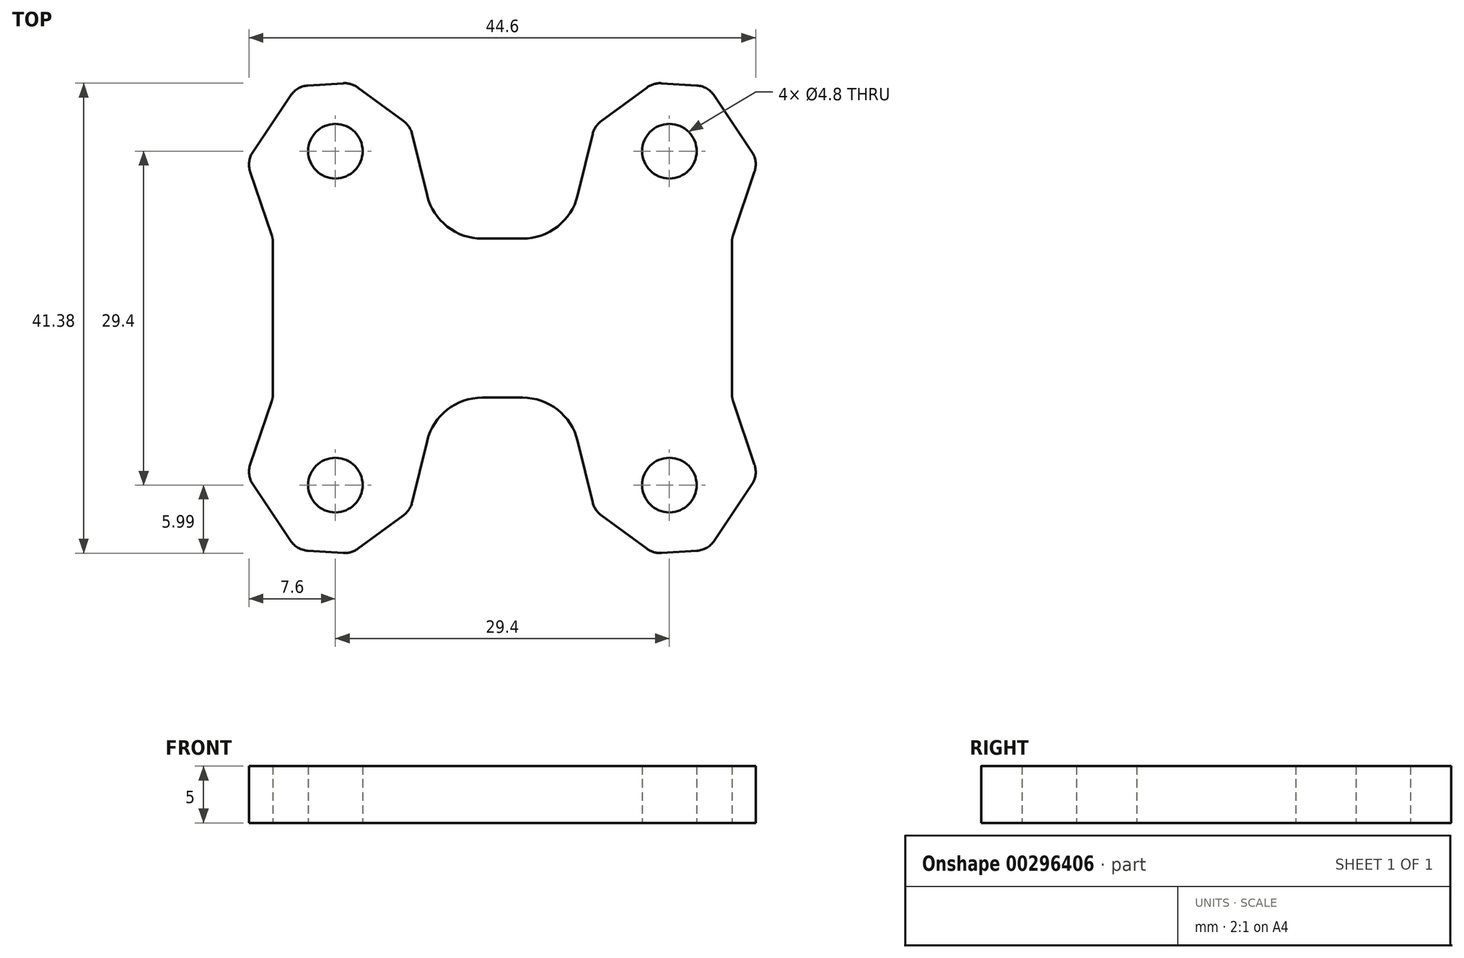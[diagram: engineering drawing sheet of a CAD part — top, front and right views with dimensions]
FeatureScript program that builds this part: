
annotation { "Feature Type Name" : "Feature", "Feature Type Description" : "" }
export const myFeature = defineFeature(function(context is Context, id is Id, definition is map)
    precondition{}
    {
        {
            var Q0;
            Q0=qCreatedBy(makeId("Top.planeOp"),FACE);
            var sketch = newSketch(context, id + "F0", { "sketchPlane" : qUnion([Q0])});
            skLineSegment(sketch, "E0.bottom", {"start": v(14.7, -14.7) * mm, "end": v(-14.7, -14.7) * mm, "construction": true});
            skLineSegment(sketch, "E0.top", {"start": v(14.7, 14.7) * mm, "end": v(-14.7, 14.7) * mm, "construction": true});
            skLineSegment(sketch, "E0.left", {"start": v(14.7, -14.7) * mm, "end": v(14.7, 14.7) * mm, "construction": true});
            skLineSegment(sketch, "E0.right", {"start": v(-14.7, -14.7) * mm, "end": v(-14.7, 14.7) * mm, "construction": true});
            skPoint(sketch, "E0.middle", {"position": v(0, 0) * mm});
            skLineSegment(sketch, "E1", {"start": v(-14.7, 5) * mm, "end": v(14.7, 5) * mm, "construction": true});
            skLineSegment(sketch, "E2.MirrorCS", {"start": v(-14.7, -5) * mm, "end": v(14.7, -5) * mm, "construction": true});
            skCircle(sketch, "E3", {"center": v(14.7, 14.7) * mm, "radius": 2.5 * mm, "construction": true});
            skCircle(sketch, "E4", {"center": v(14.7, 14.7) * mm, "radius": 9.7 * mm, "construction": true});
            skCircle(sketch, "E5.MirrorC", {"center": v(14.7, -14.7) * mm, "radius": 2.5 * mm, "construction": true});
            skCircle(sketch, "E6.MirrorC", {"center": v(14.7, -14.7) * mm, "radius": 9.7 * mm, "construction": true});
            skCircle(sketch, "E7.MirrorC", {"center": v(-14.7, 14.7) * mm, "radius": 9.7 * mm, "construction": true});
            skCircle(sketch, "E8.MirrorC", {"center": v(-14.7, 14.7) * mm, "radius": 2.5 * mm, "construction": true});
            skCircle(sketch, "E9.MirrorC", {"center": v(-14.7, -14.7) * mm, "radius": 9.7 * mm, "construction": true});
            skCircle(sketch, "E10.MirrorC", {"center": v(-14.7, -14.7) * mm, "radius": 2.5 * mm, "construction": true});
            skLineSegment(sketch, "E11", {"start": v(0, 7) * mm, "end": v(5.7, 7) * mm});
            skLineSegment(sketch, "E12", {"start": v(5.7, 7) * mm, "end": v(9.11, 21) * mm});
            skLineSegment(sketch, "E13", {"start": v(9.11, 21) * mm, "end": v(24.6, 20) * mm});
            skLineSegment(sketch, "E14", {"start": v(24.6, 20) * mm, "end": v(20.2, 7) * mm});
            skLineSegment(sketch, "E15", {"start": v(20.2, 7) * mm, "end": v(20.2, 0) * mm});
            skLineSegment(sketch, "E16", {"start": v(20.2, 0) * mm, "end": v(0, 0) * mm});
            skLineSegment(sketch, "E17", {"start": v(0, 7) * mm, "end": v(0, 0) * mm});
            skCircle(sketch, "E18", {"center": v(14.7, 14.7) * mm, "radius": 2.4 * mm});
            skSolve(sketch);
        }
        {
            var Q0;
            Q0=makeQuery(id+"F0.imprint","IMPRINT",FACE,{"disambiguationData":[TD([[makeQuery(id+"F0.imprint","IMPRINT",EDGE,{"derivedFrom":sQuery(id+"F0.wireOp",EDGE,"E11")}),-1.0]])]});
            extrude(context, id + "F1", {"entities" : qUnion([Q0]), "depth" : 5 * mm, "offsetDistance" : 25 * mm});
        }
        {
            var Q0;
            Q0=makeQuery(id+"F1.opExtrude","SWEPT_BODY",BODY,{"disambiguationData":[OSD([sQuery(id+"F0.wireOp",EDGE,"E11"),sQuery(id+"F0.wireOp",EDGE,"E12"),sQuery(id+"F0.wireOp",EDGE,"E13"),sQuery(id+"F0.wireOp",EDGE,"E14"),sQuery(id+"F0.wireOp",EDGE,"E15"),sQuery(id+"F0.wireOp",EDGE,"E16"),sQuery(id+"F0.wireOp",EDGE,"E17"),sQuery(id+"F0.wireOp",EDGE,"E18")])]});
            var Q1;
            Q1=makeQuery(id+"F1.opExtrude","SWEPT_FACE",FACE,{"disambiguationData":[OSD([sQuery(id+"F0.wireOp",EDGE,"E16")])]});
            mirror(context, id + "F2", {"operationType" : NewBodyOperationType.ADD, "entities" : qUnion([Q0]), "mirrorPlane" : qUnion([Q1])});
        }
        {
            var Q0;
            Q0=makeQuery(id+"F1.opExtrude","SWEPT_BODY",BODY,{"disambiguationData":[OSD([sQuery(id+"F0.wireOp",EDGE,"E11"),sQuery(id+"F0.wireOp",EDGE,"E12"),sQuery(id+"F0.wireOp",EDGE,"E13"),sQuery(id+"F0.wireOp",EDGE,"E14"),sQuery(id+"F0.wireOp",EDGE,"E15"),sQuery(id+"F0.wireOp",EDGE,"E16"),sQuery(id+"F0.wireOp",EDGE,"E17"),sQuery(id+"F0.wireOp",EDGE,"E18")])]});
            var Q1;
            {var subQ0=makeQuery(id+"F1.opExtrude","SWEPT_FACE",FACE,{"disambiguationData":[OSD([sQuery(id+"F0.wireOp",EDGE,"E17")])]});Q1=makeQuery(id+"F2.boolean.opBoolean","MERGE",FACE,{"derivedFrom":[subQ0,makeQuery(id+"F2.opPattern","COPY",FACE,{"derivedFrom":subQ0,"instanceName":"1"})]});}
            mirror(context, id + "F3", {"operationType" : NewBodyOperationType.ADD, "entities" : qUnion([Q0]), "mirrorPlane" : qUnion([Q1])});
        }
        {
            var Q0;
            Q0=makeQuery(id+"F1.opExtrude","SWEPT_EDGE",EDGE,{"disambiguationData":[OSD([sQuery(id+"F0.wireOp",EDGE,"E13"),sQuery(id+"F0.wireOp",EDGE,"E14")])]});
            var Q1;
            Q1=makeQuery(id+"F2.opPattern","COPY",EDGE,{"derivedFrom":makeQuery(id+"F1.opExtrude","SWEPT_EDGE",EDGE,{"disambiguationData":[OSD([sQuery(id+"F0.wireOp",EDGE,"E13"),sQuery(id+"F0.wireOp",EDGE,"E14")])]}),"instanceName":"1"});
            var Q2;
            Q2=makeQuery(id+"F2.opPattern","COPY",EDGE,{"derivedFrom":makeQuery(id+"F1.opExtrude","SWEPT_EDGE",EDGE,{"disambiguationData":[OSD([sQuery(id+"F0.wireOp",EDGE,"E12"),sQuery(id+"F0.wireOp",EDGE,"E13")])]}),"instanceName":"1"});
            var Q3;
            Q3=makeQuery(id+"F3.opPattern","COPY",EDGE,{"derivedFrom":makeQuery(id+"F2.opPattern","COPY",EDGE,{"derivedFrom":makeQuery(id+"F1.opExtrude","SWEPT_EDGE",EDGE,{"disambiguationData":[OSD([sQuery(id+"F0.wireOp",EDGE,"E12"),sQuery(id+"F0.wireOp",EDGE,"E13")])]}),"instanceName":"1"}),"instanceName":"1"});
            var Q4;
            Q4=makeQuery(id+"F3.opPattern","COPY",EDGE,{"derivedFrom":makeQuery(id+"F2.opPattern","COPY",EDGE,{"derivedFrom":makeQuery(id+"F1.opExtrude","SWEPT_EDGE",EDGE,{"disambiguationData":[OSD([sQuery(id+"F0.wireOp",EDGE,"E13"),sQuery(id+"F0.wireOp",EDGE,"E14")])]}),"instanceName":"1"}),"instanceName":"1"});
            var Q5;
            Q5=makeQuery(id+"F3.opPattern","COPY",EDGE,{"derivedFrom":makeQuery(id+"F1.opExtrude","SWEPT_EDGE",EDGE,{"disambiguationData":[OSD([sQuery(id+"F0.wireOp",EDGE,"E13"),sQuery(id+"F0.wireOp",EDGE,"E14")])]}),"instanceName":"1"});
            var Q6;
            Q6=makeQuery(id+"F3.opPattern","COPY",EDGE,{"derivedFrom":makeQuery(id+"F1.opExtrude","SWEPT_EDGE",EDGE,{"disambiguationData":[OSD([sQuery(id+"F0.wireOp",EDGE,"E12"),sQuery(id+"F0.wireOp",EDGE,"E13")])]}),"instanceName":"1"});
            var Q7;
            Q7=makeQuery(id+"F1.opExtrude","SWEPT_EDGE",EDGE,{"disambiguationData":[OSD([sQuery(id+"F0.wireOp",EDGE,"E12"),sQuery(id+"F0.wireOp",EDGE,"E13")])]});
            chamfer(context, id + "F4", {"entities" : qUnion([Q0, Q1, Q2, Q3, Q4, Q5, Q6, Q7]), "width" : 5 * mm, "tangentPropagation" : true});
        }
        {
            var Q0;
            Q0=makeQuery(id+"F3.opPattern","COPY",EDGE,{"derivedFrom":makeQuery(id+"F1.opExtrude","SWEPT_EDGE",EDGE,{"disambiguationData":[OSD([sQuery(id+"F0.wireOp",EDGE,"E11"),sQuery(id+"F0.wireOp",EDGE,"E12")])]}),"instanceName":"1"});
            var Q1;
            Q1=makeQuery(id+"F1.opExtrude","SWEPT_EDGE",EDGE,{"disambiguationData":[OSD([sQuery(id+"F0.wireOp",EDGE,"E11"),sQuery(id+"F0.wireOp",EDGE,"E12")])]});
            var Q2;
            Q2=makeQuery(id+"F2.opPattern","COPY",EDGE,{"derivedFrom":makeQuery(id+"F1.opExtrude","SWEPT_EDGE",EDGE,{"disambiguationData":[OSD([sQuery(id+"F0.wireOp",EDGE,"E11"),sQuery(id+"F0.wireOp",EDGE,"E12")])]}),"instanceName":"1"});
            var Q3;
            Q3=makeQuery(id+"F3.opPattern","COPY",EDGE,{"derivedFrom":makeQuery(id+"F2.opPattern","COPY",EDGE,{"derivedFrom":makeQuery(id+"F1.opExtrude","SWEPT_EDGE",EDGE,{"disambiguationData":[OSD([sQuery(id+"F0.wireOp",EDGE,"E11"),sQuery(id+"F0.wireOp",EDGE,"E12")])]}),"instanceName":"1"}),"instanceName":"1"});
            fillet(context, id + "F5", {"entities" : qUnion([Q0, Q1, Q2, Q3]), "radius" : 5 * mm, "tangentPropagation" : true, "allowEdgeOverflow" : false});
        }
        {
            var Q0;
            {var subQ0=sQuery(id+"F0.wireOp",EDGE,"E12");Q0=makeQuery(id+"F4.opChamfer","BLEND_EDGE",EDGE,{"blendedFrom":[makeQuery(id+"F1.opExtrude","SWEPT_EDGE",EDGE,{"disambiguationData":[OSD([subQ0,sQuery(id+"F0.wireOp",EDGE,"E13")])]}),makeQuery(id+"F1.opExtrude","SWEPT_FACE",FACE,{"disambiguationData":[OSD([subQ0])]})],"blendedInto":[makeQuery(id+"F1.opExtrude","SWEPT_FACE",FACE,{"disambiguationData":[OSD([subQ0])]})]});}
            var Q1;
            {var subQ0=sQuery(id+"F0.wireOp",EDGE,"E13");Q1=makeQuery(id+"F4.opChamfer","BLEND_EDGE",EDGE,{"blendedFrom":[makeQuery(id+"F1.opExtrude","SWEPT_EDGE",EDGE,{"disambiguationData":[OSD([sQuery(id+"F0.wireOp",EDGE,"E12"),subQ0])]}),makeQuery(id+"F1.opExtrude","SWEPT_FACE",FACE,{"disambiguationData":[OSD([subQ0])]})],"blendedInto":[makeQuery(id+"F1.opExtrude","SWEPT_FACE",FACE,{"disambiguationData":[OSD([subQ0])]})]});}
            var Q2;
            {var subQ0=sQuery(id+"F0.wireOp",EDGE,"E13");Q2=makeQuery(id+"F4.opChamfer","BLEND_EDGE",EDGE,{"blendedFrom":[makeQuery(id+"F1.opExtrude","SWEPT_EDGE",EDGE,{"disambiguationData":[OSD([subQ0,sQuery(id+"F0.wireOp",EDGE,"E14")])]}),makeQuery(id+"F1.opExtrude","SWEPT_FACE",FACE,{"disambiguationData":[OSD([subQ0])]})],"blendedInto":[makeQuery(id+"F1.opExtrude","SWEPT_FACE",FACE,{"disambiguationData":[OSD([subQ0])]})]});}
            var Q3;
            Q3=makeQuery(id+"F1.opExtrude","SWEPT_EDGE",EDGE,{"disambiguationData":[OSD([sQuery(id+"F0.wireOp",EDGE,"E14"),sQuery(id+"F0.wireOp",EDGE,"E15")])]});
            var Q4;
            Q4=makeQuery(id+"F2.opPattern","COPY",EDGE,{"derivedFrom":makeQuery(id+"F1.opExtrude","SWEPT_EDGE",EDGE,{"disambiguationData":[OSD([sQuery(id+"F0.wireOp",EDGE,"E14"),sQuery(id+"F0.wireOp",EDGE,"E15")])]}),"instanceName":"1"});
            var Q5;
            {var subQ0=sQuery(id+"F0.wireOp",EDGE,"E14");Q5=makeQuery(id+"F4.opChamfer","BLEND_EDGE",EDGE,{"blendedFrom":[makeQuery(id+"F2.opPattern","COPY",EDGE,{"derivedFrom":makeQuery(id+"F1.opExtrude","SWEPT_EDGE",EDGE,{"disambiguationData":[OSD([sQuery(id+"F0.wireOp",EDGE,"E13"),subQ0])]}),"instanceName":"1"}),makeQuery(id+"F2.opPattern","COPY",FACE,{"derivedFrom":makeQuery(id+"F1.opExtrude","SWEPT_FACE",FACE,{"disambiguationData":[OSD([subQ0])]}),"instanceName":"1"})],"blendedInto":[makeQuery(id+"F2.opPattern","COPY",FACE,{"derivedFrom":makeQuery(id+"F1.opExtrude","SWEPT_FACE",FACE,{"disambiguationData":[OSD([subQ0])]}),"instanceName":"1"})]});}
            var Q6;
            {var subQ0=sQuery(id+"F0.wireOp",EDGE,"E13");Q6=makeQuery(id+"F4.opChamfer","BLEND_EDGE",EDGE,{"blendedFrom":[makeQuery(id+"F2.opPattern","COPY",EDGE,{"derivedFrom":makeQuery(id+"F1.opExtrude","SWEPT_EDGE",EDGE,{"disambiguationData":[OSD([subQ0,sQuery(id+"F0.wireOp",EDGE,"E14")])]}),"instanceName":"1"}),makeQuery(id+"F2.opPattern","COPY",FACE,{"derivedFrom":makeQuery(id+"F1.opExtrude","SWEPT_FACE",FACE,{"disambiguationData":[OSD([subQ0])]}),"instanceName":"1"})],"blendedInto":[makeQuery(id+"F2.opPattern","COPY",FACE,{"derivedFrom":makeQuery(id+"F1.opExtrude","SWEPT_FACE",FACE,{"disambiguationData":[OSD([subQ0])]}),"instanceName":"1"})]});}
            var Q7;
            {var subQ0=sQuery(id+"F0.wireOp",EDGE,"E13");Q7=makeQuery(id+"F4.opChamfer","BLEND_EDGE",EDGE,{"blendedFrom":[makeQuery(id+"F2.opPattern","COPY",EDGE,{"derivedFrom":makeQuery(id+"F1.opExtrude","SWEPT_EDGE",EDGE,{"disambiguationData":[OSD([sQuery(id+"F0.wireOp",EDGE,"E12"),subQ0])]}),"instanceName":"1"}),makeQuery(id+"F2.opPattern","COPY",FACE,{"derivedFrom":makeQuery(id+"F1.opExtrude","SWEPT_FACE",FACE,{"disambiguationData":[OSD([subQ0])]}),"instanceName":"1"})],"blendedInto":[makeQuery(id+"F2.opPattern","COPY",FACE,{"derivedFrom":makeQuery(id+"F1.opExtrude","SWEPT_FACE",FACE,{"disambiguationData":[OSD([subQ0])]}),"instanceName":"1"})]});}
            var Q8;
            {var subQ0=sQuery(id+"F0.wireOp",EDGE,"E12");Q8=makeQuery(id+"F4.opChamfer","BLEND_EDGE",EDGE,{"blendedFrom":[makeQuery(id+"F2.opPattern","COPY",EDGE,{"derivedFrom":makeQuery(id+"F1.opExtrude","SWEPT_EDGE",EDGE,{"disambiguationData":[OSD([subQ0,sQuery(id+"F0.wireOp",EDGE,"E13")])]}),"instanceName":"1"}),makeQuery(id+"F2.opPattern","COPY",FACE,{"derivedFrom":makeQuery(id+"F1.opExtrude","SWEPT_FACE",FACE,{"disambiguationData":[OSD([subQ0])]}),"instanceName":"1"})],"blendedInto":[makeQuery(id+"F2.opPattern","COPY",FACE,{"derivedFrom":makeQuery(id+"F1.opExtrude","SWEPT_FACE",FACE,{"disambiguationData":[OSD([subQ0])]}),"instanceName":"1"})]});}
            var Q9;
            {var subQ0=sQuery(id+"F0.wireOp",EDGE,"E12");Q9=makeQuery(id+"F4.opChamfer","BLEND_EDGE",EDGE,{"blendedFrom":[makeQuery(id+"F3.opPattern","COPY",EDGE,{"derivedFrom":makeQuery(id+"F2.opPattern","COPY",EDGE,{"derivedFrom":makeQuery(id+"F1.opExtrude","SWEPT_EDGE",EDGE,{"disambiguationData":[OSD([subQ0,sQuery(id+"F0.wireOp",EDGE,"E13")])]}),"instanceName":"1"}),"instanceName":"1"}),makeQuery(id+"F3.opPattern","COPY",FACE,{"derivedFrom":makeQuery(id+"F2.opPattern","COPY",FACE,{"derivedFrom":makeQuery(id+"F1.opExtrude","SWEPT_FACE",FACE,{"disambiguationData":[OSD([subQ0])]}),"instanceName":"1"}),"instanceName":"1"})],"blendedInto":[makeQuery(id+"F3.opPattern","COPY",FACE,{"derivedFrom":makeQuery(id+"F2.opPattern","COPY",FACE,{"derivedFrom":makeQuery(id+"F1.opExtrude","SWEPT_FACE",FACE,{"disambiguationData":[OSD([subQ0])]}),"instanceName":"1"}),"instanceName":"1"})]});}
            var Q10;
            {var subQ0=sQuery(id+"F0.wireOp",EDGE,"E13");Q10=makeQuery(id+"F4.opChamfer","BLEND_EDGE",EDGE,{"blendedFrom":[makeQuery(id+"F3.opPattern","COPY",EDGE,{"derivedFrom":makeQuery(id+"F2.opPattern","COPY",EDGE,{"derivedFrom":makeQuery(id+"F1.opExtrude","SWEPT_EDGE",EDGE,{"disambiguationData":[OSD([sQuery(id+"F0.wireOp",EDGE,"E12"),subQ0])]}),"instanceName":"1"}),"instanceName":"1"}),makeQuery(id+"F3.opPattern","COPY",FACE,{"derivedFrom":makeQuery(id+"F2.opPattern","COPY",FACE,{"derivedFrom":makeQuery(id+"F1.opExtrude","SWEPT_FACE",FACE,{"disambiguationData":[OSD([subQ0])]}),"instanceName":"1"}),"instanceName":"1"})],"blendedInto":[makeQuery(id+"F3.opPattern","COPY",FACE,{"derivedFrom":makeQuery(id+"F2.opPattern","COPY",FACE,{"derivedFrom":makeQuery(id+"F1.opExtrude","SWEPT_FACE",FACE,{"disambiguationData":[OSD([subQ0])]}),"instanceName":"1"}),"instanceName":"1"})]});}
            var Q11;
            {var subQ0=sQuery(id+"F0.wireOp",EDGE,"E13");Q11=makeQuery(id+"F4.opChamfer","BLEND_EDGE",EDGE,{"blendedFrom":[makeQuery(id+"F3.opPattern","COPY",EDGE,{"derivedFrom":makeQuery(id+"F2.opPattern","COPY",EDGE,{"derivedFrom":makeQuery(id+"F1.opExtrude","SWEPT_EDGE",EDGE,{"disambiguationData":[OSD([subQ0,sQuery(id+"F0.wireOp",EDGE,"E14")])]}),"instanceName":"1"}),"instanceName":"1"}),makeQuery(id+"F3.opPattern","COPY",FACE,{"derivedFrom":makeQuery(id+"F2.opPattern","COPY",FACE,{"derivedFrom":makeQuery(id+"F1.opExtrude","SWEPT_FACE",FACE,{"disambiguationData":[OSD([subQ0])]}),"instanceName":"1"}),"instanceName":"1"})],"blendedInto":[makeQuery(id+"F3.opPattern","COPY",FACE,{"derivedFrom":makeQuery(id+"F2.opPattern","COPY",FACE,{"derivedFrom":makeQuery(id+"F1.opExtrude","SWEPT_FACE",FACE,{"disambiguationData":[OSD([subQ0])]}),"instanceName":"1"}),"instanceName":"1"})]});}
            var Q12;
            {var subQ0=sQuery(id+"F0.wireOp",EDGE,"E14");Q12=makeQuery(id+"F4.opChamfer","BLEND_EDGE",EDGE,{"blendedFrom":[makeQuery(id+"F3.opPattern","COPY",EDGE,{"derivedFrom":makeQuery(id+"F2.opPattern","COPY",EDGE,{"derivedFrom":makeQuery(id+"F1.opExtrude","SWEPT_EDGE",EDGE,{"disambiguationData":[OSD([sQuery(id+"F0.wireOp",EDGE,"E13"),subQ0])]}),"instanceName":"1"}),"instanceName":"1"}),makeQuery(id+"F3.opPattern","COPY",FACE,{"derivedFrom":makeQuery(id+"F2.opPattern","COPY",FACE,{"derivedFrom":makeQuery(id+"F1.opExtrude","SWEPT_FACE",FACE,{"disambiguationData":[OSD([subQ0])]}),"instanceName":"1"}),"instanceName":"1"})],"blendedInto":[makeQuery(id+"F3.opPattern","COPY",FACE,{"derivedFrom":makeQuery(id+"F2.opPattern","COPY",FACE,{"derivedFrom":makeQuery(id+"F1.opExtrude","SWEPT_FACE",FACE,{"disambiguationData":[OSD([subQ0])]}),"instanceName":"1"}),"instanceName":"1"})]});}
            var Q13;
            Q13=makeQuery(id+"F3.opPattern","COPY",EDGE,{"derivedFrom":makeQuery(id+"F2.opPattern","COPY",EDGE,{"derivedFrom":makeQuery(id+"F1.opExtrude","SWEPT_EDGE",EDGE,{"disambiguationData":[OSD([sQuery(id+"F0.wireOp",EDGE,"E14"),sQuery(id+"F0.wireOp",EDGE,"E15")])]}),"instanceName":"1"}),"instanceName":"1"});
            var Q14;
            Q14=makeQuery(id+"F3.opPattern","COPY",EDGE,{"derivedFrom":makeQuery(id+"F1.opExtrude","SWEPT_EDGE",EDGE,{"disambiguationData":[OSD([sQuery(id+"F0.wireOp",EDGE,"E14"),sQuery(id+"F0.wireOp",EDGE,"E15")])]}),"instanceName":"1"});
            var Q15;
            {var subQ0=sQuery(id+"F0.wireOp",EDGE,"E14");Q15=makeQuery(id+"F4.opChamfer","BLEND_EDGE",EDGE,{"blendedFrom":[makeQuery(id+"F3.opPattern","COPY",EDGE,{"derivedFrom":makeQuery(id+"F1.opExtrude","SWEPT_EDGE",EDGE,{"disambiguationData":[OSD([sQuery(id+"F0.wireOp",EDGE,"E13"),subQ0])]}),"instanceName":"1"}),makeQuery(id+"F3.opPattern","COPY",FACE,{"derivedFrom":makeQuery(id+"F1.opExtrude","SWEPT_FACE",FACE,{"disambiguationData":[OSD([subQ0])]}),"instanceName":"1"})],"blendedInto":[makeQuery(id+"F3.opPattern","COPY",FACE,{"derivedFrom":makeQuery(id+"F1.opExtrude","SWEPT_FACE",FACE,{"disambiguationData":[OSD([subQ0])]}),"instanceName":"1"})]});}
            var Q16;
            {var subQ0=sQuery(id+"F0.wireOp",EDGE,"E13");Q16=makeQuery(id+"F4.opChamfer","BLEND_EDGE",EDGE,{"blendedFrom":[makeQuery(id+"F3.opPattern","COPY",EDGE,{"derivedFrom":makeQuery(id+"F1.opExtrude","SWEPT_EDGE",EDGE,{"disambiguationData":[OSD([subQ0,sQuery(id+"F0.wireOp",EDGE,"E14")])]}),"instanceName":"1"}),makeQuery(id+"F3.opPattern","COPY",FACE,{"derivedFrom":makeQuery(id+"F1.opExtrude","SWEPT_FACE",FACE,{"disambiguationData":[OSD([subQ0])]}),"instanceName":"1"})],"blendedInto":[makeQuery(id+"F3.opPattern","COPY",FACE,{"derivedFrom":makeQuery(id+"F1.opExtrude","SWEPT_FACE",FACE,{"disambiguationData":[OSD([subQ0])]}),"instanceName":"1"})]});}
            var Q17;
            {var subQ0=sQuery(id+"F0.wireOp",EDGE,"E12");Q17=makeQuery(id+"F4.opChamfer","BLEND_EDGE",EDGE,{"blendedFrom":[makeQuery(id+"F3.opPattern","COPY",EDGE,{"derivedFrom":makeQuery(id+"F1.opExtrude","SWEPT_EDGE",EDGE,{"disambiguationData":[OSD([subQ0,sQuery(id+"F0.wireOp",EDGE,"E13")])]}),"instanceName":"1"}),makeQuery(id+"F3.opPattern","COPY",FACE,{"derivedFrom":makeQuery(id+"F1.opExtrude","SWEPT_FACE",FACE,{"disambiguationData":[OSD([subQ0])]}),"instanceName":"1"})],"blendedInto":[makeQuery(id+"F3.opPattern","COPY",FACE,{"derivedFrom":makeQuery(id+"F1.opExtrude","SWEPT_FACE",FACE,{"disambiguationData":[OSD([subQ0])]}),"instanceName":"1"})]});}
            var Q18;
            {var subQ0=sQuery(id+"F0.wireOp",EDGE,"E14");Q18=makeQuery(id+"F4.opChamfer","BLEND_EDGE",EDGE,{"blendedFrom":[makeQuery(id+"F1.opExtrude","SWEPT_EDGE",EDGE,{"disambiguationData":[OSD([sQuery(id+"F0.wireOp",EDGE,"E13"),subQ0])]}),makeQuery(id+"F1.opExtrude","SWEPT_FACE",FACE,{"disambiguationData":[OSD([subQ0])]})],"blendedInto":[makeQuery(id+"F1.opExtrude","SWEPT_FACE",FACE,{"disambiguationData":[OSD([subQ0])]})]});}
            var Q19;
            {var subQ0=sQuery(id+"F0.wireOp",EDGE,"E13");Q19=makeQuery(id+"F4.opChamfer","BLEND_EDGE",EDGE,{"blendedFrom":[makeQuery(id+"F3.opPattern","COPY",EDGE,{"derivedFrom":makeQuery(id+"F1.opExtrude","SWEPT_EDGE",EDGE,{"disambiguationData":[OSD([sQuery(id+"F0.wireOp",EDGE,"E12"),subQ0])]}),"instanceName":"1"}),makeQuery(id+"F3.opPattern","COPY",FACE,{"derivedFrom":makeQuery(id+"F1.opExtrude","SWEPT_FACE",FACE,{"disambiguationData":[OSD([subQ0])]}),"instanceName":"1"})],"blendedInto":[makeQuery(id+"F3.opPattern","COPY",FACE,{"derivedFrom":makeQuery(id+"F1.opExtrude","SWEPT_FACE",FACE,{"disambiguationData":[OSD([subQ0])]}),"instanceName":"1"})]});}
            fillet(context, id + "F6", {"entities" : qUnion([Q0, Q1, Q2, Q3, Q4, Q5, Q6, Q7, Q8, Q9, Q10, Q11, Q12, Q13, Q14, Q15, Q16, Q17, Q18, Q19]), "radius" : 2 * mm, "tangentPropagation" : true, "allowEdgeOverflow" : false});
        }
    });
